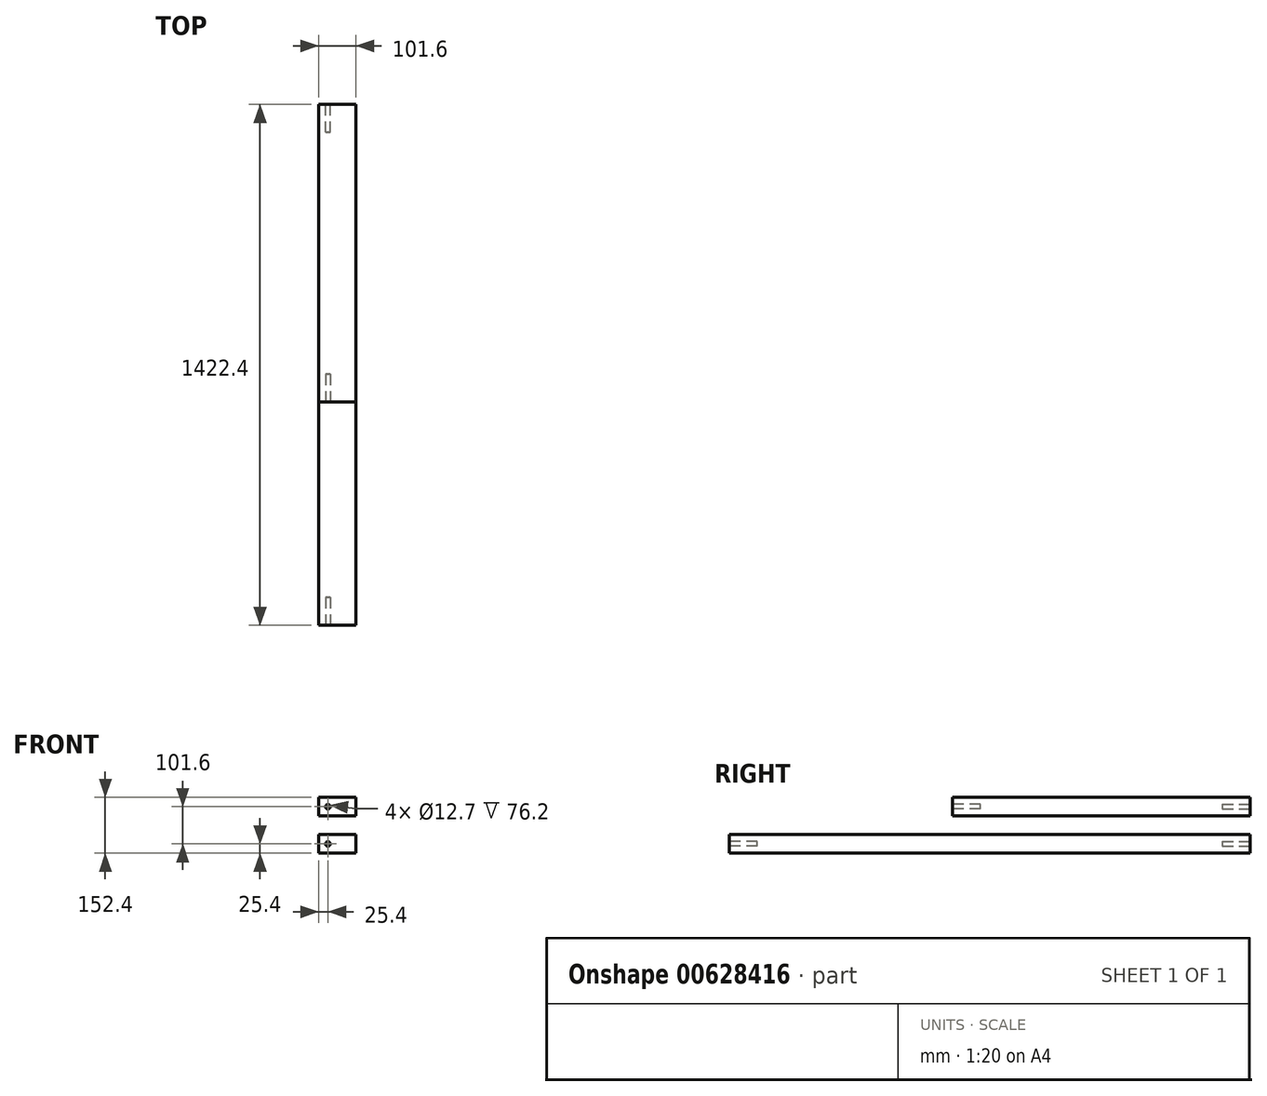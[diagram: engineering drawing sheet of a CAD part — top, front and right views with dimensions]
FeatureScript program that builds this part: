
annotation { "Feature Type Name" : "Feature", "Feature Type Description" : "" }
export const myFeature = defineFeature(function(context is Context, id is Id, definition is map)
    precondition{}
    {
        {
            var Q0;
            Q0=qCreatedBy(makeId("Front.planeOp"),FACE);
            var sketch = newSketch(context, id + "F0", { "sketchPlane" : qUnion([Q0])});
            skLineSegment(sketch, "E0.bottom", {"start": v(-50.8, 50.8) * mm, "end": v(50.8, 50.8) * mm});
            skLineSegment(sketch, "E0.top", {"start": v(-50.8, 0) * mm, "end": v(50.8, 0) * mm});
            skLineSegment(sketch, "E0.left", {"start": v(-50.8, 50.8) * mm, "end": v(-50.8, 0) * mm});
            skLineSegment(sketch, "E0.right", {"start": v(50.8, 50.8) * mm, "end": v(50.8, 0) * mm});
            skSolve(sketch);
        }
        {
            var Q0;
            Q0=makeQuery(id+"F0.imprint","IMPRINT",FACE,{"disambiguationData":[TD([[makeQuery(id+"F0.imprint","IMPRINT",EDGE,{"derivedFrom":sQuery(id+"F0.wireOp",EDGE,"E0.bottom")}),-1.0]])]});
            extrude(context, id + "F1", {"entities" : qUnion([Q0]), "depth" : 812.8 * mm, "offsetDistance" : 25.4 * mm});
        }
        {
            var Q0;
            Q0=qCreatedBy(makeId("Front.planeOp"),FACE);
            var sketch = newSketch(context, id + "F2", { "sketchPlane" : qUnion([Q0])});
            skLineSegment(sketch, "E1.bottom", {"start": v(-50.8, -50.8) * mm, "end": v(50.8, -50.8) * mm});
            skLineSegment(sketch, "E1.top", {"start": v(-50.8, -101.6) * mm, "end": v(50.8, -101.6) * mm});
            skLineSegment(sketch, "E1.left", {"start": v(-50.8, -50.8) * mm, "end": v(-50.8, -101.6) * mm});
            skLineSegment(sketch, "E1.right", {"start": v(50.8, -50.8) * mm, "end": v(50.8, -101.6) * mm});
            skSolve(sketch);
        }
        {
            var Q0;
            Q0 = qSketchRegion(id + "F2", true);
            extrude(context, id + "F3", {"entities" : qUnion([Q0]), "depth" : 1422.4 * mm, "offsetDistance" : 25.4 * mm});
        }
        {
            var Q0;
            Q0=makeQuery(id+"F1.opExtrude","CAP_FACE",FACE,{"disambiguationData":[OSD([sQuery(id+"F0.wireOp",EDGE,"E0.bottom"),sQuery(id+"F0.wireOp",EDGE,"E0.top"),sQuery(id+"F0.wireOp",EDGE,"E0.left"),sQuery(id+"F0.wireOp",EDGE,"E0.right")])],"isStart":false});
            var sketch = newSketch(context, id + "F4", { "sketchPlane" : qUnion([Q0])});
            skCircle(sketch, "E2", {"center": v(-25.4, 25.4) * mm, "radius": 6.35 * mm});
            skSolve(sketch);
        }
        {
            var Q0;
            Q0 = qSketchRegion(id + "F4", true);
            extrude(context, id + "F5", {"entities" : qUnion([Q0]), "operationType" : NewBodyOperationType.REMOVE, "oppositeDirection" : true, "depth" : 76.2 * mm, "offsetDistance" : 25.4 * mm});
        }
        {
            var Q0;
            Q0=makeQuery(id+"F1.opExtrude","CAP_FACE",FACE,{"disambiguationData":[OSD([sQuery(id+"F0.wireOp",EDGE,"E0.bottom"),sQuery(id+"F0.wireOp",EDGE,"E0.top"),sQuery(id+"F0.wireOp",EDGE,"E0.left"),sQuery(id+"F0.wireOp",EDGE,"E0.right")])],"isStart":true});
            var sketch = newSketch(context, id + "F6", { "sketchPlane" : qUnion([Q0])});
            skCircle(sketch, "E3", {"center": v(25.4, 25.4) * mm, "radius": 6.35 * mm});
            skSolve(sketch);
        }
        {
            var Q0;
            Q0=makeQuery(id+"F6.imprint","IMPRINT",FACE,{"disambiguationData":[TD([[makeQuery(id+"F6.imprint","IMPRINT",EDGE,{"derivedFrom":sQuery(id+"F6.wireOp",EDGE,"E3")}),1.0]])]});
            extrude(context, id + "F7", {"entities" : qUnion([Q0]), "operationType" : NewBodyOperationType.REMOVE, "oppositeDirection" : true, "depth" : 76.2 * mm, "offsetDistance" : 25.4 * mm});
        }
        {
            var Q0;
            Q0=makeQuery(id+"F3.opExtrude","CAP_FACE",FACE,{"disambiguationData":[OSD([sQuery(id+"F2.wireOp",EDGE,"E1.bottom"),sQuery(id+"F2.wireOp",EDGE,"E1.top"),sQuery(id+"F2.wireOp",EDGE,"E1.left"),sQuery(id+"F2.wireOp",EDGE,"E1.right")])],"isStart":false});
            var sketch = newSketch(context, id + "F8", { "sketchPlane" : qUnion([Q0])});
            skCircle(sketch, "E4", {"center": v(-25.4, -76.2) * mm, "radius": 6.35 * mm});
            skSolve(sketch);
        }
        {
            var Q0;
            Q0 = qSketchRegion(id + "F8", true);
            extrude(context, id + "F9", {"entities" : qUnion([Q0]), "operationType" : NewBodyOperationType.REMOVE, "oppositeDirection" : true, "depth" : 76.2 * mm, "offsetDistance" : 25.4 * mm});
        }
        {
            var Q0;
            Q0=makeQuery(id+"F3.opExtrude","CAP_FACE",FACE,{"disambiguationData":[OSD([sQuery(id+"F2.wireOp",EDGE,"E1.bottom"),sQuery(id+"F2.wireOp",EDGE,"E1.top"),sQuery(id+"F2.wireOp",EDGE,"E1.left"),sQuery(id+"F2.wireOp",EDGE,"E1.right")])],"isStart":true});
            var sketch = newSketch(context, id + "F10", { "sketchPlane" : qUnion([Q0])});
            skCircle(sketch, "E5", {"center": v(25.4, -76.2) * mm, "radius": 6.35 * mm});
            skSolve(sketch);
        }
        {
            var Q0;
            Q0 = qSketchRegion(id + "F10", true);
            extrude(context, id + "F11", {"entities" : qUnion([Q0]), "operationType" : NewBodyOperationType.REMOVE, "oppositeDirection" : true, "depth" : 76.2 * mm, "offsetDistance" : 25.4 * mm});
        }
    });
